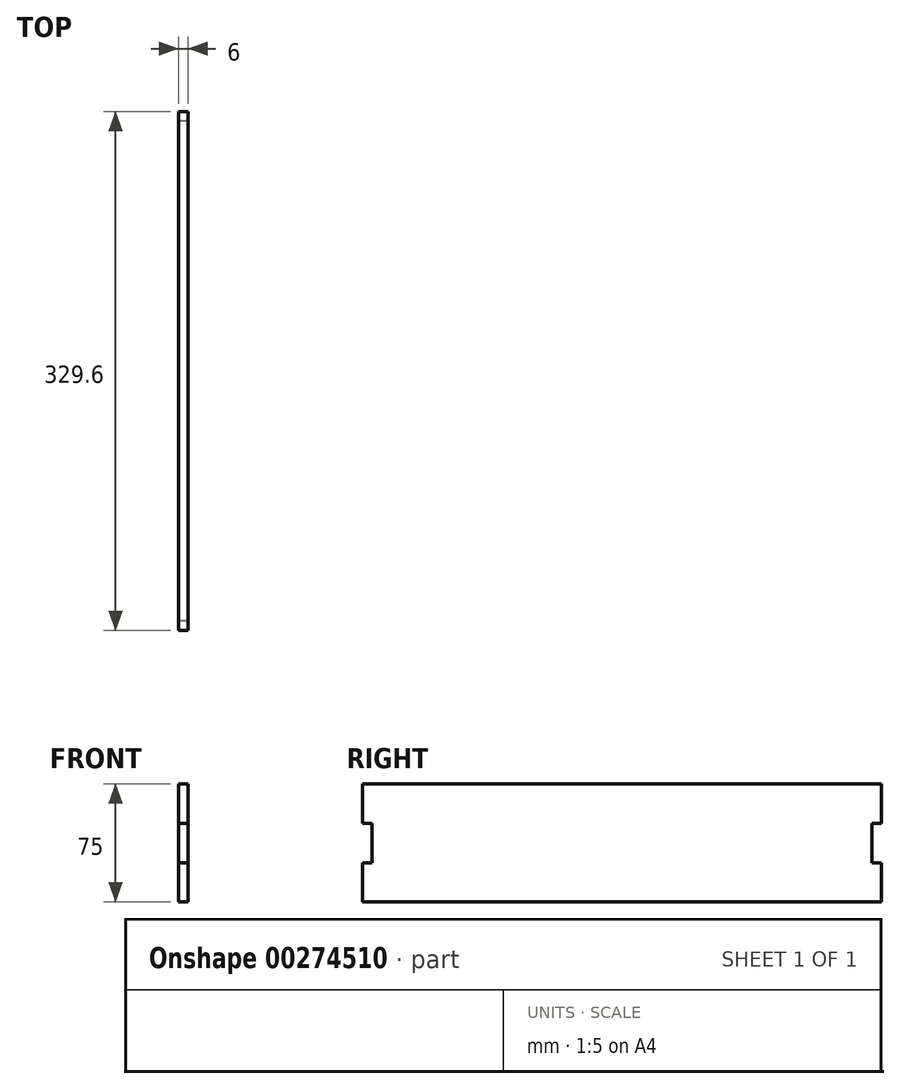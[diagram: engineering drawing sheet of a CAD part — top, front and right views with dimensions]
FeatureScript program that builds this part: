
annotation { "Feature Type Name" : "Feature", "Feature Type Description" : "" }
export const myFeature = defineFeature(function(context is Context, id is Id, definition is map)
    precondition{}
    {
        {
            var Q0;
            Q0=qCreatedBy(makeId("Right.planeOp"),FACE);
            var sketch = newSketch(context, id + "F0", { "sketchPlane" : qUnion([Q0])});
            skLineSegment(sketch, "E0.bottom", {"start": v(-256.02, 58.03) * mm, "end": v(61.58, 58.03) * mm});
            skLineSegment(sketch, "E0.top", {"start": v(-256.02, -16.97) * mm, "end": v(61.58, -16.97) * mm});
            skLineSegment(sketch, "E1", {"start": v(-256.02, 58.03) * mm, "end": v(-262.02, 58.03) * mm});
            skLineSegment(sketch, "E2", {"start": v(-262.02, 58.03) * mm, "end": v(-262.02, 33.03) * mm});
            skLineSegment(sketch, "E3", {"start": v(-262.02, 33.03) * mm, "end": v(-256.02, 33.03) * mm});
            skLineSegment(sketch, "E4", {"start": v(-256.02, 33.03) * mm, "end": v(-256.02, 8.03) * mm});
            skLineSegment(sketch, "E5", {"start": v(-256.02, 8.03) * mm, "end": v(-262.02, 8.03) * mm});
            skLineSegment(sketch, "E6", {"start": v(-262.02, 8.03) * mm, "end": v(-262.02, -16.97) * mm});
            skLineSegment(sketch, "E7", {"start": v(-262.02, -16.97) * mm, "end": v(-256.02, -16.97) * mm});
            skLineSegment(sketch, "E8", {"start": v(61.58, 58.03) * mm, "end": v(67.58, 58.03) * mm});
            skLineSegment(sketch, "E9", {"start": v(67.58, 58.03) * mm, "end": v(67.58, 33.03) * mm});
            skLineSegment(sketch, "E10", {"start": v(67.58, 8.03) * mm, "end": v(67.58, -16.97) * mm});
            skLineSegment(sketch, "E11", {"start": v(67.58, -16.97) * mm, "end": v(61.58, -16.97) * mm});
            skLineSegment(sketch, "E12", {"start": v(67.58, 8.03) * mm, "end": v(61.58, 8.03) * mm});
            skLineSegment(sketch, "E13", {"start": v(61.58, 8.03) * mm, "end": v(61.58, 33.03) * mm});
            skLineSegment(sketch, "E14", {"start": v(61.58, 33.03) * mm, "end": v(67.58, 33.03) * mm});
            skSolve(sketch);
        }
        {
            var Q0;
            Q0=makeQuery(id+"F0.imprint","IMPRINT",FACE,{"disambiguationData":[TD([[makeQuery(id+"F0.imprint","IMPRINT",EDGE,{"derivedFrom":sQuery(id+"F0.wireOp",EDGE,"E0.bottom")}),-1.0]])]});
            extrude(context, id + "F1", {"entities" : qUnion([Q0]), "depth" : 6 * mm});
        }
    });
